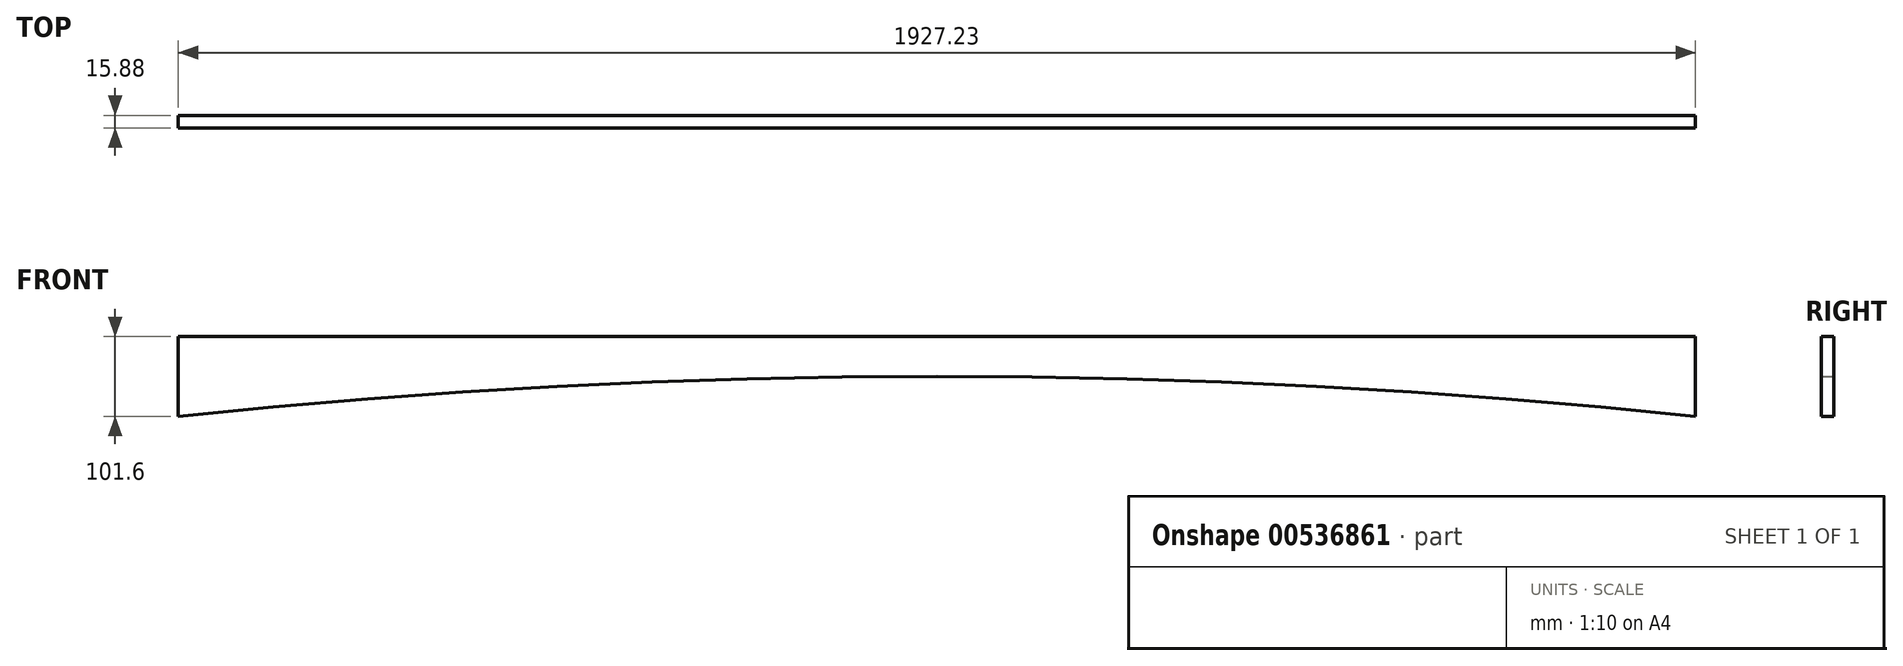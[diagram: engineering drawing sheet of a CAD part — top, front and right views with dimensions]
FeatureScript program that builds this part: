
annotation { "Feature Type Name" : "Feature", "Feature Type Description" : "" }
export const myFeature = defineFeature(function(context is Context, id is Id, definition is map)
    precondition{}
    {
        {
            var Q0;
            Q0=qCreatedBy(makeId("Front.planeOp"),FACE);
            var sketch = newSketch(context, id + "F0", { "sketchPlane" : qUnion([Q0])});
            skLineSegment(sketch, "E0", {"start": v(-63.4, 32.74) * mm, "end": v(1863.82, 32.74) * mm});
            skLineSegment(sketch, "E1", {"start": v(1863.82, 32.74) * mm, "end": v(1863.82, -43.46) * mm});
            skLineSegment(sketch, "E2", {"start": v(-63.4, 32.74) * mm, "end": v(-63.4, -43.46) * mm});
            skArc(sketch, "E3", {"start": v(1863.82, -43.46) * mm, "mid": v(900.2, 7.34) * mm, "end": v(-63.4, -43.46) * mm});
            skPoint(sketch, "E4.start.orphan", {"position": v(900.2, 32.74) * mm});
            skSolve(sketch);
        }
        {
            var Q0;
            Q0 = qSketchRegion(id + "F0", true);
            extrude(context, id + "F1", {"entities" : qUnion([Q0]), "depth" : 25.4 * mm, "offsetDistance" : 25.4 * mm});
        }
        {
            var Q0;
            Q0=makeQuery(id+"F1.opExtrude","SWEPT_BODY",BODY,{"disambiguationData":[OSD([sQuery(id+"F0.wireOp",EDGE,"E0"),sQuery(id+"F0.wireOp",EDGE,"E1"),sQuery(id+"F0.wireOp",EDGE,"E2"),sQuery(id+"F0.wireOp",EDGE,"E3")])]});
            deleteBodies(context, id + "F2", {"entities" : qUnion([Q0])});
        }
        {
            var Q0;
            Q0=qCreatedBy(makeId("Front.planeOp"),FACE);
            var sketch = newSketch(context, id + "F3", { "sketchPlane" : qUnion([Q0])});
            skLineSegment(sketch, "E5", {"start": v(-68.44, 30.76) * mm, "end": v(1858.79, 30.76) * mm});
            skLineSegment(sketch, "E6", {"start": v(1858.79, 30.76) * mm, "end": v(1858.79, -70.84) * mm});
            skLineSegment(sketch, "E7", {"start": v(-68.44, 30.76) * mm, "end": v(-68.44, -70.84) * mm});
            skLineSegment(sketch, "E8", {"start": v(-68.44, -70.84) * mm, "end": v(-68.44, 30.76) * mm});
            skArc(sketch, "E9", {"start": v(1858.79, -70.84) * mm, "mid": v(895.18, -20.04) * mm, "end": v(-68.44, -70.84) * mm});
            skPoint(sketch, "E10.start.orphan", {"position": v(895.18, 30.76) * mm});
            skSolve(sketch);
        }
        {
            var Q0;
            Q0=makeQuery(id+"F3.imprint","IMPRINT",FACE,{"disambiguationData":[TD([[makeQuery(id+"F3.imprint","IMPRINT",EDGE,{"derivedFrom":sQuery(id+"F3.wireOp",EDGE,"E5")}),-1.0]])]});
            extrude(context, id + "F4", {"entities" : qUnion([Q0]), "depth" : 15.88 * mm, "offsetDistance" : 25.4 * mm});
        }
    });
